# Revit family: Hager-Volta-IP30-Flush_mounted-sistema-NoHosted-PT-pt
name_source: partatom
category: Electrical Equipment
units: mm (PartAtom-declared; Revit-internal decimal feet)

## family parameters
Always vertical = Yes
Cut with Voids When Loaded = No
Panel Configuration = Two Columns, Circuits Across
Part Type = Panelboard
Room Calculation Point = No
Round Connector Dimension = Use Diameter
Shared = No
Work Plane-Based = Yes

## types (10) — shared parameters
Default Elevation = 1219 mm
EF000003 - Método de montagem = EV000383 - Montagem embutida (gesso)
EF000007 - Cor = EV000202 - Branco
EF000008 - Largura = 348 mm  [stored 1.14173 ft]
EF000049 - Profundidade = 94 mm  [stored 0.308399 ft]
EF000116 - Número RAL = 9010
EF000118 - Com tampa de montagem = No
EF000218 - Profundidade incorporada = 90 mm  [stored 0.295276 ft]
EF000339 - Tipo de difusor = EV004216 - Porta
EF000846 - Largura para embutir = 335 mm  [stored 1.09908 ft]
EF001062 - Versão EMC = No
EF001088 - Extensão possível = Yes
EF001131 - Profundidade interior = 92 mm
EF001134 - Calha DIN = Yes
EF002950 - Largura em número de módulos = 12
EF004462 - Tipo de fecho = EV000154 - Outro
EF005474 - Grau de proteção (IP) = EV006410 - IP30
EF006306 - Com fecho = No
EF009212 - Tipo de tampa = EV009916 - Com recuo
EF015776 - Borne de terra = Yes
EF015777 - Borne de neutro = No
EF015941 - Porta para passagem de sinal = No
HG000001 - Número de colunas = 1
HG000002 - Com porta ou tampa = Yes
HG000003 - Gama = Volta
HG000005 - Espessura = 3 mm  [stored 0.00984252 ft]
HG000006 - Encastrado = Yes
HG000009 - Porta dupla = No
HG000010 - Portas assimétricas = No
HG000011 - Filas vazias desde da parte de baixo = No
HG000017 - Distância entre polos = 18 mm  [stored 0.0590551 ft]
Manufacturer = Hager
Type Comments = Volta
zero-valued in all types: HG000007 - Número de colunas vazias, HG000008 - Número de filas vazias

## per-type parameters (varying)
| type | EF000040 - Altura | EF000266 - Número de linhas | EF000332 - Altura embutida | EF001596 - Material do corpo | EF006244 - Tampa/porta transparente | HG000004 - Referência do Fabricante | Model |
| Montagem embutida IP30 L348 A356 P94.5 12 unidade de divisão - VU12EP | 356 mm | 1 | 321 mm | EV000139 - Plástico | No | VU12EP | VU12EP |
| Montagem embutida IP30 L348 A356 P94.5 12 unidade de divisão - VU12ET | 356 mm | 1 | 321 mm | EV000139 - Plástico | Yes | VU12ET | VU12ET |
| Montagem embutida IP30 L348 A505.5 P94.5 12 unidade de divisão - VU24EP | 506 mm | 2 | 471 mm | EV000139 - Plástico | No | VU24EP | VU24EP |
| Montagem embutida IP30 L348 A505.5 P94.5 12 unidade de divisão - VU24ET | 506 mm | 2 | 471 mm | EV000139 - Plástico | Yes | VU24ET | VU24ET |
| Montagem embutida IP30 L348 A630.5 P94.5 12 unidade de divisão - VU36EP | 630 mm | 3 | 596 mm | EV000139 - Plástico | No | VU36EP | VU36EP |
| Montagem embutida IP30 L348 A630.5 P94.5 12 unidade de divisão - VU36ET | 630 mm | 3 | 596 mm | EV000139 - Plástico | Yes | VU36ET | VU36ET |
| Montagem embutida IP30 L348 A755.5 P94.5 12 unidade de divisão - VU48EP | 756 mm | 4 | 721 mm | EV000139 - Plástico | No | VU48EP | VU48EP |
| Montagem embutida IP30 L348 A755.5 P94.5 12 unidade de divisão - VU48ET | 756 mm | 4 | 721 mm | EV000139 - Plástico | Yes | VU48ET | VU48ET |
| Montagem embutida IP30 L348 A880.5 P94.5 12 unidade de divisão - VU60EP | 880 mm  [stored 2.88714 ft] | 5 | 846 mm  [stored 2.77559 ft] | EV000154 - Outro | No | VU60EP | VU60EP |
| Montagem embutida IP30 L348 A880.5 P94.5 12 unidade de divisão - VU60ET | 880 mm  [stored 2.88714 ft] | 5 | 846 mm  [stored 2.77559 ft] | EV000154 - Outro | Yes | VU60ET | VU60ET |

note: [stored X ft] marks values corroborated as IEEE doubles in the binary element streams (Revit-internal decimal feet)

## geometry (parser evidence)
native form markers: Sweep x13
no freeform markers — native parametric forms only
